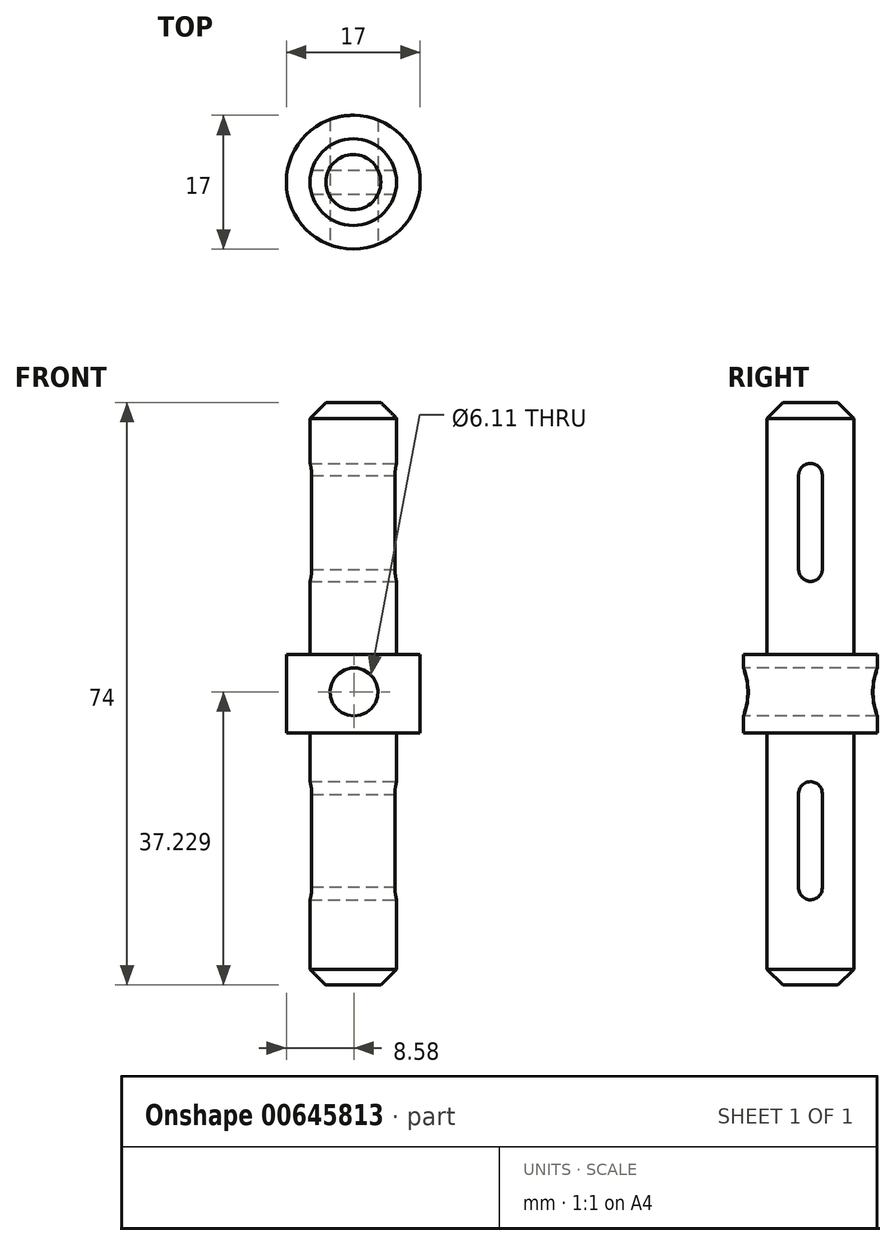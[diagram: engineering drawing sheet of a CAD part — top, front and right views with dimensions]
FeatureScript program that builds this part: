
annotation { "Feature Type Name" : "Feature", "Feature Type Description" : "" }
export const myFeature = defineFeature(function(context is Context, id is Id, definition is map)
    precondition{}
    {
        {
            var Q0;
            Q0=qCreatedBy(makeId("Top.planeOp"),FACE);
            var sketch = newSketch(context, id + "F0", { "sketchPlane" : qUnion([Q0])});
            skCircle(sketch, "E0", {"center": v(-34.66, 0) * mm, "radius": 8.5 * mm});
            skSolve(sketch);
        }
        {
            var Q0;
            Q0=makeQuery(id+"F0.imprint","IMPRINT",FACE,{"disambiguationData":[TD([[makeQuery(id+"F0.imprint","IMPRINT",EDGE,{"derivedFrom":sQuery(id+"F0.wireOp",EDGE,"E0")}),1.0]])]});
            extrude(context, id + "F1", {"entities" : qUnion([Q0]), "depth" : 10 * mm, "offsetDistance" : 25 * mm});
        }
        {
            var Q0;
            Q0=makeQuery(id+"F1.opExtrude","CAP_FACE",FACE,{"disambiguationData":[OSD([sQuery(id+"F0.wireOp",EDGE,"E0")])],"isStart":false});
            var sketch = newSketch(context, id + "F2", { "sketchPlane" : qUnion([Q0])});
            skCircle(sketch, "E1", {"center": v(-34.66, 0) * mm, "radius": 5.5 * mm});
            skSolve(sketch);
        }
        {
            var Q0;
            Q0=makeQuery(id+"F2.imprint","IMPRINT",FACE,{"disambiguationData":[TD([[makeQuery(id+"F2.imprint","IMPRINT",EDGE,{"derivedFrom":sQuery(id+"F2.wireOp",EDGE,"E1")}),1.0]])]});
            extrude(context, id + "F3", {"entities" : qUnion([Q0]), "operationType" : NewBodyOperationType.ADD, "depth" : 32 * mm, "offsetDistance" : 25 * mm});
        }
        {
            var Q0;
            Q0=makeQuery(id+"F1.opExtrude","CAP_FACE",FACE,{"disambiguationData":[OSD([sQuery(id+"F0.wireOp",EDGE,"E0")])],"isStart":true});
            var sketch = newSketch(context, id + "F4", { "sketchPlane" : qUnion([Q0])});
            skCircle(sketch, "E2", {"center": v(-34.66, 0) * mm, "radius": 5.5 * mm});
            skSolve(sketch);
        }
        {
            var Q0;
            Q0 = qSketchRegion(id + "F4", true);
            extrude(context, id + "F5", {"entities" : qUnion([Q0]), "operationType" : NewBodyOperationType.ADD, "depth" : 32 * mm, "offsetDistance" : 25 * mm});
        }
        {
            var Q0;
            Q0=makeQuery(id+"F3.opExtrude","CAP_FACE",FACE,{"disambiguationData":[OSD([sQuery(id+"F2.wireOp",EDGE,"E1")])],"isStart":false});
            chamfer(context, id + "F6", {"entities" : qUnion([Q0]), "width" : 2 * mm, "tangentPropagation" : true});
        }
        {
            var Q0;
            Q0=makeQuery(id+"F5.opExtrude","CAP_EDGE",EDGE,{"disambiguationData":[OSD([sQuery(id+"F4.wireOp",EDGE,"E2")])],"isStart":false});
            chamfer(context, id + "F7", {"entities" : qUnion([Q0]), "width" : 2 * mm, "tangentPropagation" : true});
        }
        {
            var Q0;
            Q0=qCreatedBy(makeId("Front.planeOp"),FACE);
            var sketch = newSketch(context, id + "F8", { "sketchPlane" : qUnion([Q0])});
            skCircle(sketch, "E3", {"center": v(-34.58, 5.23) * mm, "radius": 3.05 * mm});
            skSolve(sketch);
        }
        {
            var Q0;
            Q0 = qSketchRegion(id + "F8", true);
            extrude(context, id + "F9", {"entities" : qUnion([Q0]), "operationType" : NewBodyOperationType.REMOVE, "endBound" : BoundingType.THROUGH_ALL, "oppositeDirection" : true, "depth" : 25 * mm, "offsetDistance" : 25 * mm, "hasSecondDirection" : true, "secondDirectionBound" : SecondDirectionBoundingType.THROUGH_ALL, "secondDirectionOppositeDirection" : false, "secondDirectionDepth" : 25 * mm});
        }
        {
            var Q0;
            Q0=qCreatedBy(makeId("Right.planeOp"),FACE);
            var sketch = newSketch(context, id + "F10", { "sketchPlane" : qUnion([Q0])});
            skArc(sketch, "E4", {"start": v(1.5, 32.77) * mm, "mid": v(-0.02, 34.27) * mm, "end": v(-1.5, 32.73) * mm});
            skArc(sketch, "E5", {"start": v(-1.5, 20.81) * mm, "mid": v(-0.02, 19.27) * mm, "end": v(1.5, 20.77) * mm});
            skLineSegment(sketch, "E6", {"start": v(-1.5, 32.73) * mm, "end": v(-1.5, 20.73) * mm});
            skLineSegment(sketch, "E7", {"start": v(1.5, 20.77) * mm, "end": v(1.5, 32.77) * mm});
            skPoint(sketch, "E8.start.orphan", {"position": v(0, 26.77) * mm});
            skPoint(sketch, "E9.trimOffspring.end.orphan", {"position": v(0, 10) * mm});
            skPoint(sketch, "E10.start.orphan", {"position": v(0, 43.54) * mm});
            skSolve(sketch);
        }
        {
            var Q0;
            Q0 = qSketchRegion(id + "F10", true);
            extrude(context, id + "F11", {"entities" : qUnion([Q0]), "operationType" : NewBodyOperationType.REMOVE, "endBound" : BoundingType.THROUGH_ALL, "oppositeDirection" : true, "depth" : 25 * mm, "offsetDistance" : 25 * mm});
        }
        {
            var Q0;
            Q0=qCreatedBy(makeId("Right.planeOp"),FACE);
            var sketch = newSketch(context, id + "F12", { "sketchPlane" : qUnion([Q0])});
            skArc(sketch, "E11", {"start": v(-1.5, -19.53) * mm, "mid": v(-0.07, -21.16) * mm, "end": v(1.5, -19.66) * mm});
            skArc(sketch, "E12", {"start": v(1.5, -7.66) * mm, "mid": v(-0.07, -6.16) * mm, "end": v(-1.5, -7.8) * mm});
            skLineSegment(sketch, "E13", {"start": v(-1.5, -19.8) * mm, "end": v(-1.5, -7.8) * mm});
            skLineSegment(sketch, "E14", {"start": v(1.5, -19.66) * mm, "end": v(1.5, -7.66) * mm});
            skPoint(sketch, "E15.start.orphan", {"position": v(0, -13.66) * mm});
            skPoint(sketch, "E16.start.orphan", {"position": v(0, -27.32) * mm});
            skPoint(sketch, "E17.trimOffspring.end.orphan", {"position": v(0, 0) * mm});
            skSolve(sketch);
        }
        {
            var Q0;
            Q0 = qSketchRegion(id + "F12", true);
            extrude(context, id + "F13", {"entities" : qUnion([Q0]), "operationType" : NewBodyOperationType.REMOVE, "endBound" : BoundingType.THROUGH_ALL, "oppositeDirection" : true, "depth" : 25 * mm, "offsetDistance" : 25 * mm});
        }
    });
